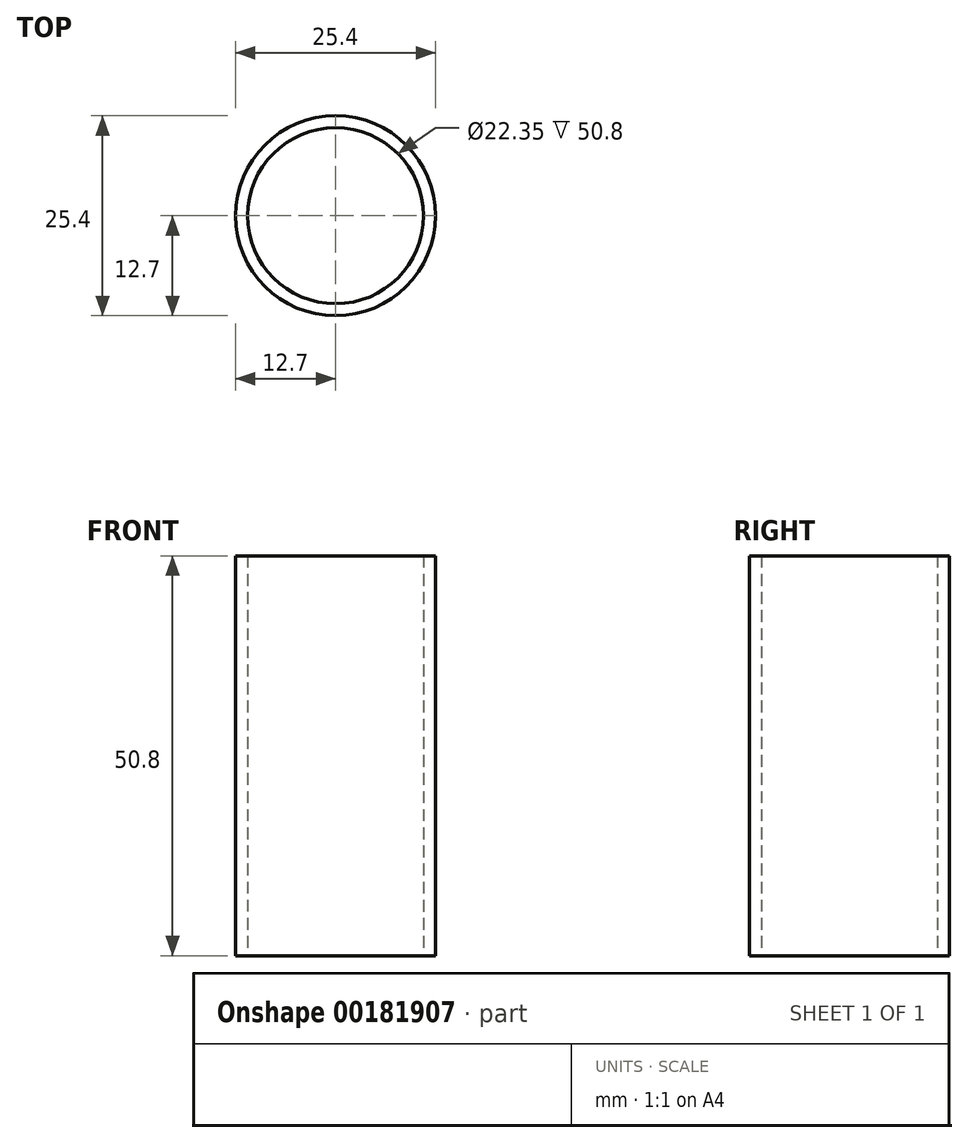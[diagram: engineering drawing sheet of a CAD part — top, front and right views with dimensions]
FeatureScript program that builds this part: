
annotation { "Feature Type Name" : "Feature", "Feature Type Description" : "" }
export const myFeature = defineFeature(function(context is Context, id is Id, definition is map)
    precondition{}
    {
        {
            var Q0;
            Q0=qCreatedBy(makeId("Top.planeOp"),FACE);
            var sketch = newSketch(context, id + "F0", { "sketchPlane" : qUnion([Q0])});
            skCircle(sketch, "E0", {"center": v(0, 0) * mm, "radius": 12.7 * mm});
            skCircle(sketch, "E1", {"center": v(0, 0) * mm, "radius": 11.18 * mm});
            skLineSegment(sketch, "E2", {"start": v(11.18, 0) * mm, "end": v(12.7, 0) * mm, "construction": true});
            skSolve(sketch);
        }
        {
            var Q0;
            Q0 = qSketchRegion(id + "F0", true);
            extrude(context, id + "F1", {"entities" : qUnion([Q0]), "depth" : 50.8 * mm});
        }
    });
